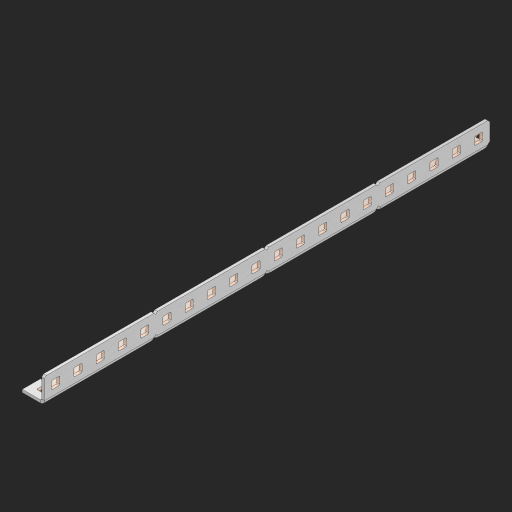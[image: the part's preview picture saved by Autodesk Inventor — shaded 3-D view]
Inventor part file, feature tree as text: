
AUTODESK INVENTOR PART (.ipt)
format: ipt  version: 2023 (Build 270158000, 158)  size: 994,304 bytes
history: native  units: in
note: dims shown in document units (in); Inventor stores cm internally (conversion verified against a paired STEP export)
features: other x208, extrude x58, sheet_metal_op x11, sketch x10, pattern_linear x2, mirror x1, chamfer x1
ambient origin geometry x8: Origin, YZ Plane, XZ Plane, XY Plane, X Axis, Y Axis, Z Axis, Center Point
bodies: Solid1 (feature_tree), Body (feature_tree)
feature tree (291):
  other  "Alu Half C 1x2x1x20"
  other  "Table"
  other  "Alu C 1x2x1x35"
  other  "Alu C 1x2x1x34"
  other  "Alu C 1x2x1x33"
  other  "Alu C 1x2x1x32"
  other  "Alu C 1x2x1x31"
  other  "Alu C 1x2x1x30"
  other  "Alu C 1x2x1x29"
  other  "Alu C 1x2x1x28"
  other  "Alu C 1x2x1x27"
  other  "Alu C 1x2x1x26"
  other  "Alu C 1x2x1x25"
  other  "Alu C 1x2x1x24"
  other  "Alu C 1x2x1x23"
  other  "Alu C 1x2x1x22"
  other  "Alu C 1x2x1x21"
  other  "Alu C 1x2x1x20"
  other  "Alu C 1x2x1x19"
  other  "Alu C 1x2x1x18"
  other  "Alu C 1x2x1x17"
  other  "Alu C 1x2x1x16"
  other  "Alu C 1x2x1x15"
  other  "Alu C 1x2x1x14"
  other  "Alu C 1x2x1x13"
  other  "Alu C 1x2x1x12"
  other  "Alu C 1x2x1x11"
  other  "Alu C 1x2x1x10"
  other  "Alu C 1x2x1x9"
  other  "Alu C 1x2x1x8"
  other  "Alu C 1x2x1x7"
  other  "Alu C 1x2x1x6"
  other  "Alu C 1x2x1x5"
  other  "Alu C 1x2x1x4"
  other  "Alu C 1x2x1x3"
  other  "Alu C 1x2x1x2"
  other  "Alu C 1x2x1x1"
  other  "Steel C 1x2x1x35"
  other  "Steel C 1x2x1x34"
  other  "Steel C 1x2x1x33"
  other  "Steel C 1x2x1x32"
  other  "Steel C 1x2x1x31"
  other  "Steel C 1x2x1x30"
  other  "Steel C 1x2x1x29"
  other  "Steel C 1x2x1x28"
  other  "Steel C 1x2x1x27"
  other  "Steel C 1x2x1x26"
  other  "Steel C 1x2x1x25"
  other  "Steel C 1x2x1x24"
  other  "Steel C 1x2x1x23"
  other  "Steel C 1x2x1x22"
  other  "Steel C 1x2x1x21"
  other  "Steel C 1x2x1x20"
  other  "Steel C 1x2x1x19"
  other  "Steel C 1x2x1x18"
  other  "Steel C 1x2x1x17"
  other  "Steel C 1x2x1x16"
  other  "Steel C 1x2x1x15"
  other  "Steel C 1x2x1x14"
  other  "Steel C 1x2x1x13"
  other  "Steel C 1x2x1x12"
  other  "Steel C 1x2x1x11"
  other  "Steel C 1x2x1x10"
  other  "Steel C 1x2x1x9"
  other  "Steel C 1x2x1x8"
  other  "Steel C 1x2x1x7"
  other  "Steel C 1x2x1x6"
  other  "Steel C 1x2x1x5"
  other  "Steel C 1x2x1x4"
  other  "Steel C 1x2x1x3"
  other  "Steel C 1x2x1x2"
  other  "Steel C 1x2x1x1"
  other  "Alu Half C 1x2x1x35"
  other  "Alu Half C 1x2x1x34"
  other  "Alu Half C 1x2x1x33"
  other  "Alu Half C 1x2x1x32"
  other  "Alu Half C 1x2x1x31"
  other  "Alu Half C 1x2x1x30"
  other  "Alu Half C 1x2x1x29"
  other  "Alu Half C 1x2x1x28"
  other  "Alu Half C 1x2x1x27"
  other  "Alu Half C 1x2x1x26"
  other  "Alu Half C 1x2x1x25"
  other  "Alu Half C 1x2x1x24"
  other  "Alu Half C 1x2x1x23"
  other  "Alu Half C 1x2x1x22"
  other  "Alu Half C 1x2x1x21"
  other  "Alu Half C 1x2x1x19"
  other  "Alu Half C 1x2x1x18"
  other  "Alu Half C 1x2x1x17"
  other  "Alu Half C 1x2x1x16"
  other  "Alu Half C 1x2x1x15"
  other  "Alu Half C 1x2x1x14"
  other  "Alu Half C 1x2x1x13"
  other  "Alu Half C 1x2x1x12"
  other  "Alu Half C 1x2x1x11"
  other  "Alu Half C 1x2x1x10"
  other  "Alu Half C 1x2x1x9"
  other  "Alu Half C 1x2x1x8"
  other  "Alu Half C 1x2x1x7"
  other  "Alu Half C 1x2x1x6"
  other  "Alu Half C 1x2x1x5"
  other  "Alu Half C 1x2x1x4"
  other  "Alu Half C 1x2x1x3"
  other  "Alu Half C 1x2x1x2"
  other  "Alu Half C 1x2x1x1"
  other  "Steel Half C 1x2x1x35"
  other  "Steel Half C 1x2x1x34"
  other  "Steel Half C 1x2x1x33"
  other  "Steel Half C 1x2x1x32"
  other  "Steel Half C 1x2x1x31"
  other  "Steel Half C 1x2x1x30"
  other  "Steel Half C 1x2x1x29"
  other  "Steel Half C 1x2x1x28"
  other  "Steel Half C 1x2x1x27"
  other  "Steel Half C 1x2x1x26"
  other  "Steel Half C 1x2x1x25"
  other  "Steel Half C 1x2x1x24"
  other  "Steel Half C 1x2x1x23"
  other  "Steel Half C 1x2x1x22"
  other  "Steel Half C 1x2x1x21"
  other  "Steel Half C 1x2x1x20"
  other  "Steel Half C 1x2x1x19"
  other  "Steel Half C 1x2x1x18"
  other  "Steel Half C 1x2x1x17"
  other  "Steel Half C 1x2x1x16"
  other  "Steel Half C 1x2x1x15"
  other  "Steel Half C 1x2x1x14"
  other  "Steel Half C 1x2x1x13"
  other  "Steel Half C 1x2x1x12"
  other  "Steel Half C 1x2x1x11"
  other  "Steel Half C 1x2x1x10"
  other  "Steel Half C 1x2x1x9"
  other  "Steel Half C 1x2x1x8"
  other  "Steel Half C 1x2x1x7"
  other  "Steel Half C 1x2x1x6"
  other  "Steel Half C 1x2x1x5"
  other  "Steel Half C 1x2x1x4"
  other  "Steel Half C 1x2x1x3"
  other  "Steel Half C 1x2x1x2"
  other  "Steel Half C 1x2x1x1"
  sheet_metal_op  "Flanges"
  other  "Flange Pattern Plane"
  other  "Flange Pattern Sketch"
  sheet_metal_op  "Flange Pattern"
  sheet_metal_op  "Body Pattern"
  pattern_linear  "Center Pattern"  Spacing1=0.0625in  [1 undecoded]
  other  "Arc Length"
  mirror  "Notch Mirror"
  pattern_linear  "Notch Pattern"  Spacing1=0.182in  [1 undecoded]
  chamfer  "End Chamfer"
  extrude  "Half Cut"  Depth=0.02in
  sketch  "Sketch1"  dims[d0=1.0in]
  other  "Plate1"
  sketch  "Sketch2"  dims[d1=10.0in]
  other  "Plate2"
  sheet_metal_op  "Bend1"
  sheet_metal_op  "Corner1"
  sketch  "Sketch3"  dims[d2=0.0625in]
  sketch  "Sketch7"  dims[d3=0.0625in]
  other  "Srf1"
  other  "Srf2"
  sketch  "Sketch8"  dims[d4=0.0312in]
  sketch  "Sketch9"  dims[d5=0.125in]
  other  "Srf91"
  sheet_metal_op  "Body Pattern Sketch"
  other  "Srf92"
  sketch  "Sketch13"  dims[d6=0.0625in]
  sketch  "Sketch14"  dims[d7=0.5in d8=90.0deg d9=0.0312in]
  sketch  "Sketch15"  dims[d10=0.25in]
  sketch  "Sketch16"  dims[d11=0.0625in d12=0.0625in d16=0.182in d17=0.02in d18=0.0625in d19=0.0in d20=0.25in d21=0.25in d38=7.874in d40=0.5in d41=0.3937in d43=1.0in d46=0.172in d47=1.0in d48=0.0in d49=0.182in d50=0.02in d51=0.25in d52=0.25in d53=0.0625in d54=0.0in d55=0.172in d56=1.0in d57=0.0in d58=0.25in d60=7.874in d62=0.5in d63=0.3937in d65=0.5in d85=0.1473in d86=0.1782in d88=0.04in d89=0.0625in d90=0.0in d91=0.04in d92=0.0491in d95=2.5in d96=0.04in d97=0.25in d98=45.0deg d99=0.25in d100=0.5in d101=0.0in d102=2.497in d106=0.182in d107=0.02in d108=0.5in d109=0.5in d110=0.0625in d111=0.0in d112=0.172in d113=0.5in d114=0.0in d117=0.5in d118=0.5in d119=0.5in]
  other  "Srf786"
  other  "Srf823"
  other  "Srf824"
  other  "Srf825"
  other  "Srf826"
  other  "Srf827"
  other  "Srf828"
  other  "Srf829"
  other  "Srf856"
  other  "Srf857"
  other  "Srf858"
  other  "Srf859"
  other  "Srf860"
  other  "Srf861"
  other  "Srf862"
  other  "Srf889"
  other  "Srf890"
  other  "Srf891"
  other  "Srf892"
  other  "Srf893"
  other  "Srf894"
  other  "Srf895"
  other  "Srf896"
  other  "Srf922"
  other  "Srf923"
  other  "Srf924"
  other  "Srf925"
  other  "Srf926"
  other  "Srf959"
  other  "Srf960"
  other  "Srf961"
  other  "Srf962"
  other  "Srf963"
  other  "Srf996"
  other  "Srf997"
  other  "Srf998"
  other  "Srf999"
  other  "Srf1000"
  other  "Srf1143"
  other  "Srf1144"
  other  "Srf1145"
  other  "Srf1146"
  other  "Srf1147"
  other  "Srf1148"
  other  "Srf1199"
  other  "Srf1200"
  other  "Srf1201"
  other  "Srf1202"
  other  "Srf1203"
  other  "Srf1204"
  other  "Srf1255"
  other  "Srf1256"
  other  "Srf1257"
  other  "Srf1258"
  other  "Srf1259"
  other  "Srf1260"
  sheet_metal_op  "Flange Stamp"
  sheet_metal_op  "Flange Circle"
  sheet_metal_op  "Body Stamp"
  sheet_metal_op  "Body Circle"
  other  "Center Stamp"
  other  "Center Circle"
  sheet_metal_op  "Notch"
  extrude  "ExtrusionSrf2"  Depth=0.0625in
  extrude  "ExtrusionSrf92"  TaperAngle=0.0deg  [1 undecoded]
  extrude  "ExtrusionSrf823"  Depth=0.25in
  extrude  "ExtrusionSrf824"  Depth=0.25in
  extrude  "ExtrusionSrf825"  Depth=0.5in
  extrude  "ExtrusionSrf826"  Depth=0.5in
  extrude  "ExtrusionSrf827"  Depth=1.0in TaperAngle=0.0deg
  extrude  "ExtrusionSrf828"  Depth=0.182in
  extrude  "ExtrusionSrf829"  Depth=0.02in
  extrude  "ExtrusionSrf856"  Depth=0.25in
  extrude  "ExtrusionSrf857"  Depth=0.25in
  extrude  "ExtrusionSrf858"  Depth=0.0625in
  extrude  "ExtrusionSrf859"  TaperAngle=0.0deg  [1 undecoded]
  extrude  "ExtrusionSrf860"  Depth=0.5in
  extrude  "ExtrusionSrf861"  Depth=1.0in TaperAngle=0.0deg
  extrude  "ExtrusionSrf862"  Depth=0.25in
  extrude  "ExtrusionSrf889"  Depth=0.5in
  extrude  "ExtrusionSrf890"  Depth=0.5in
  extrude  "ExtrusionSrf891"  Depth=0.5in
  extrude  "ExtrusionSrf892"  Depth=0.5in
  extrude  "ExtrusionSrf893"  Depth=0.5in
  extrude  "ExtrusionSrf894"  Depth=0.0625in
  extrude  "ExtrusionSrf895"  TaperAngle=0.0deg  [1 undecoded]
  extrude  "ExtrusionSrf896"  Depth=0.5in
  extrude  "ExtrusionSrf922"  Depth=0.5in
  extrude  "ExtrusionSrf923"  Depth=2.5in
  extrude  "ExtrusionSrf924"  Depth=0.25in TaperAngle=45.0deg
  extrude  "ExtrusionSrf925"  Depth=0.25in
  extrude  "ExtrusionSrf926"  Depth=0.5in TaperAngle=0.0deg
  extrude  "ExtrusionSrf959"  Depth=0.5in
  extrude  "ExtrusionSrf960"  Depth=0.182in
  extrude  "ExtrusionSrf961"  Depth=0.02in
  extrude  "ExtrusionSrf962"  Depth=0.5in
  extrude  "ExtrusionSrf963"  Depth=0.5in
  extrude  "ExtrusionSrf996"  Depth=0.0625in
  extrude  "ExtrusionSrf997"  TaperAngle=0.0deg  [1 undecoded]
  extrude  "ExtrusionSrf998"  Depth=0.5in
  extrude  "ExtrusionSrf999"  Depth=0.5in TaperAngle=0.0deg
  extrude  "ExtrusionSrf1000"  Depth=0.5in
  extrude  "ExtrusionSrf1143"  Depth=0.5in
  extrude  "ExtrusionSrf1144"  Depth=0.5in
  extrude  "ExtrusionSrf1145"  [1 undecoded]
  extrude  "ExtrusionSrf1146"  [1 undecoded]
  extrude  "ExtrusionSrf1147"  [1 undecoded]
  extrude  "ExtrusionSrf1148"  [1 undecoded]
  extrude  "ExtrusionSrf1199"  [1 undecoded]
  extrude  "ExtrusionSrf1200"  [1 undecoded]
  extrude  "ExtrusionSrf1201"  [1 undecoded]
  extrude  "ExtrusionSrf1202"  [1 undecoded]
  extrude  "ExtrusionSrf1203"  [1 undecoded]
  extrude  "ExtrusionSrf1204"  [1 undecoded]
  extrude  "ExtrusionSrf1255"  [1 undecoded]
  extrude  "ExtrusionSrf1256"  [1 undecoded]
  extrude  "ExtrusionSrf1257"  [1 undecoded]
  extrude  "ExtrusionSrf1258"  [1 undecoded]
  extrude  "ExtrusionSrf1259"  [1 undecoded]
  extrude  "ExtrusionSrf1260"  [1 undecoded]
note: 22 required parameter values undecoded (feature->parameter linkage not recoverable at this tier; creation-order binding heuristic only, values carry confidence <= 0.55)
